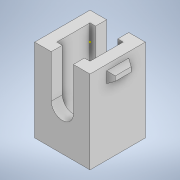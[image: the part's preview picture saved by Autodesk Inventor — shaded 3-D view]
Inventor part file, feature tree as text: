
AUTODESK INVENTOR PART (.ipt)
format: ipt  version: 2022 (Build 260153000, 153)  size: 139,264 bytes
history: native  units: in
note: dims shown in document units (in); Inventor stores cm internally (conversion verified against a paired STEP export)
features: sketch x9, extrude x4, shell x1
ambient origin geometry x8: Origin, YZ Plane, XZ Plane, XY Plane, X Axis, Y Axis, Z Axis, Center Point
bodies: Solid1 (feature_tree)
feature tree (14):
  extrude  "Extrusion1"  Depth=0.1969in
  shell  "Shell1"  Thickness=0.2953in
  sketch  "Sketch4"  dims[d4=0.0394in d10=0.0394in]
  sketch  "Sketch5"  dims[d11=0.0197in d12=-0.2061in d13=0.0394in]
  sketch  "Sketch6"  dims[d14=0.0787in d15=0.0394in]
  sketch  "Sketch7"  dims[d16=0.0787in]
  sketch  "Sketch8"  dims[d17=0.0394in]
  extrude  "Extrusion4"  Depth=0.0394in
  extrude  "Extrusion5"  Depth=0.0394in
  extrude  "Extrusion6"  Depth=0.0394in
  sketch  "Sketch1"  dims[d0=0.1969in d1=0.1969in d2=0.2953in d3=0.0in]
  sketch  "Sketch9"  dims[d18=0.0197in d19=-0.2061in]
  sketch  "Sketch10"  dims[d20=0.0787in]
  sketch  "Sketch11"  dims[d21=0.0in d22=0.0in]
